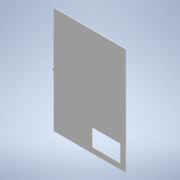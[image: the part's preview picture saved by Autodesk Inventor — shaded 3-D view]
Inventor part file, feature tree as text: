
AUTODESK INVENTOR PART (.ipt)
format: ipt  version: 2022 (Build 260153000, 153)  size: 102,912 bytes
history: native  units: in
note: dims shown in document units (in); Inventor stores cm internally (conversion verified against a paired STEP export)
features: extrude x2, sketch x2, other x1
ambient origin geometry x8: Origin, YZ Plane, XZ Plane, XY Plane, X Axis, Y Axis, Z Axis, Center Point
bodies: Solid1 (feature_tree)
feature tree (5):
  extrude  "Extrusion1"  Depth=5.9055in
  other  "Work Point1"
  extrude  "Extrusion2"  Depth=1.9685in
  sketch  "Sketch1"  dims[d0=0.2362in d1=0.0in d2=5.9055in]
  sketch  "Sketch2"  dims[d3=10.0394in d4=1.9685in d5=1.9685in d6=0.0in d7=0.0in]
